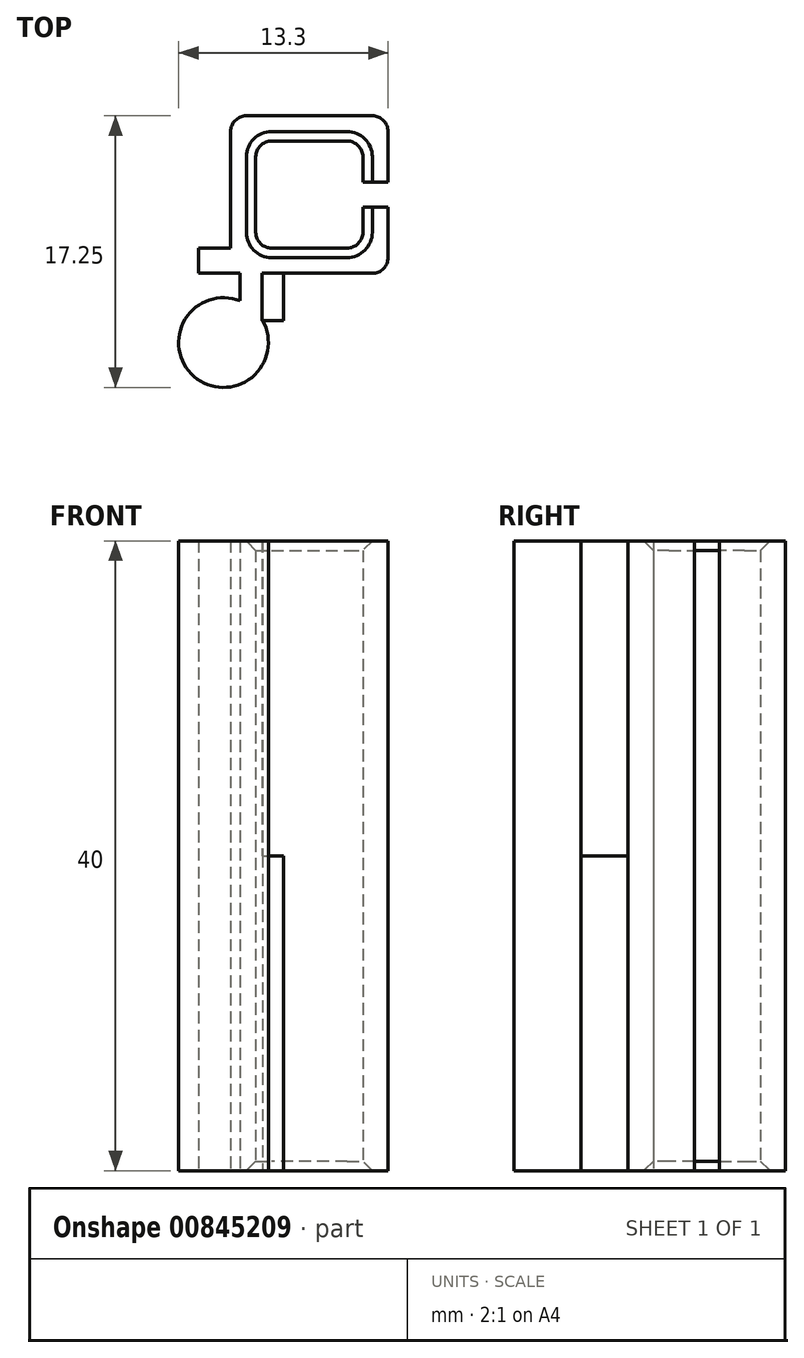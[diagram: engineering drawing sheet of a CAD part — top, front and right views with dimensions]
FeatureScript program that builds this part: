
annotation { "Feature Type Name" : "Feature", "Feature Type Description" : "" }
export const myFeature = defineFeature(function(context is Context, id is Id, definition is map)
    precondition{}
    {
        {
            var Q0;
            Q0=qCreatedBy(makeId("Top.planeOp"),FACE);
            var sketch = newSketch(context, id + "F0", { "sketchPlane" : qUnion([Q0])});
            skCircle(sketch, "E0", {"center": v(0, 0) * mm, "radius": 2.85 * mm});
            skLineSegment(sketch, "E1.bottom", {"start": v(0.45, 0) * mm, "end": v(2.45, 0) * mm});
            skLineSegment(sketch, "E1.top", {"start": v(0.45, 4.4) * mm, "end": v(2.45, 4.4) * mm});
            skLineSegment(sketch, "E1.left", {"start": v(0.45, 0) * mm, "end": v(0.45, 4.4) * mm});
            skLineSegment(sketch, "E1.right", {"start": v(2.45, 0) * mm, "end": v(2.45, 4.4) * mm});
            skLineSegment(sketch, "E2.bottom", {"start": v(0.45, 4.4) * mm, "end": v(10.45, 4.4) * mm});
            skLineSegment(sketch, "E2.top", {"start": v(0.45, 14.4) * mm, "end": v(10.45, 14.4) * mm});
            skLineSegment(sketch, "E2.left", {"start": v(0.45, 4.4) * mm, "end": v(0.45, 14.4) * mm});
            skLineSegment(sketch, "E2.right", {"start": v(10.45, 4.4) * mm, "end": v(10.45, 14.4) * mm});
            skLineSegment(sketch, "E3.bottom", {"start": v(2.05, 6) * mm, "end": v(8.85, 6) * mm});
            skLineSegment(sketch, "E3.top", {"start": v(2.05, 12.8) * mm, "end": v(8.85, 12.8) * mm});
            skLineSegment(sketch, "E3.left", {"start": v(2.05, 6) * mm, "end": v(2.05, 12.8) * mm});
            skLineSegment(sketch, "E3.right", {"start": v(8.85, 6) * mm, "end": v(8.85, 12.8) * mm});
            skLineSegment(sketch, "E4.bottom", {"start": v(8.85, 8.6) * mm, "end": v(10.45, 8.6) * mm});
            skLineSegment(sketch, "E4.top", {"start": v(8.85, 10.2) * mm, "end": v(10.45, 10.2) * mm});
            skLineSegment(sketch, "E4.left", {"start": v(8.85, 8.6) * mm, "end": v(8.85, 10.2) * mm});
            skLineSegment(sketch, "E4.right", {"start": v(10.45, 8.6) * mm, "end": v(10.45, 10.2) * mm});
            skLineSegment(sketch, "E5.bottom", {"start": v(0.45, 4.4) * mm, "end": v(1.05, 4.4) * mm});
            skLineSegment(sketch, "E5.top", {"start": v(0.45, 2.65) * mm, "end": v(1.05, 2.65) * mm});
            skLineSegment(sketch, "E5.left", {"start": v(0.45, 4.4) * mm, "end": v(0.45, 2.65) * mm});
            skLineSegment(sketch, "E5.right", {"start": v(1.05, 4.4) * mm, "end": v(1.05, 2.65) * mm});
            skLineSegment(sketch, "E6.bottom", {"start": v(0.45, 4.4) * mm, "end": v(-1.6, 4.4) * mm});
            skLineSegment(sketch, "E6.top", {"start": v(0.45, 6) * mm, "end": v(-1.6, 6) * mm});
            skLineSegment(sketch, "E6.left", {"start": v(0.45, 4.4) * mm, "end": v(0.45, 6) * mm});
            skLineSegment(sketch, "E6.right", {"start": v(-1.6, 4.4) * mm, "end": v(-1.6, 6) * mm});
            skLineSegment(sketch, "E7.bottom", {"start": v(3.8, 4.4) * mm, "end": v(5.4, 4.4) * mm});
            skLineSegment(sketch, "E7.top", {"start": v(3.8, -1) * mm, "end": v(5.4, -1) * mm});
            skLineSegment(sketch, "E7.left", {"start": v(3.8, 4.4) * mm, "end": v(3.8, -1) * mm});
            skLineSegment(sketch, "E7.right", {"start": v(5.4, 4.4) * mm, "end": v(5.4, -1) * mm});
            skLineSegment(sketch, "E8", {"start": v(2.45, 1.4) * mm, "end": v(3.8, 1.4) * mm});
            skCircle(sketch, "E9", {"center": v(0, 0) * mm, "radius": 3 * mm, "construction": true});
            skLineSegment(sketch, "E10.bottom", {"start": v(3.4, 4) * mm, "end": v(-6.83, 4) * mm, "construction": true});
            skLineSegment(sketch, "E10.top", {"start": v(3.4, -6.58) * mm, "end": v(-6.83, -6.58) * mm, "construction": true});
            skLineSegment(sketch, "E10.left", {"start": v(3.4, 4) * mm, "end": v(3.4, -6.58) * mm, "construction": true});
            skLineSegment(sketch, "E10.right", {"start": v(-6.83, 4) * mm, "end": v(-6.83, -6.58) * mm, "construction": true});
            skLineSegment(sketch, "E11", {"start": v(10.45, 9.4) * mm, "end": v(8.85, 9.4) * mm, "construction": true});
            skSolve(sketch);
        }
        {
            var Q0;
            Q0=makeQuery(id+"F0.imprint","IMPRINT",FACE,{"disambiguationData":[TD([[makeQuery(id+"F0.imprint","IMPRINT",EDGE,{"derivedFrom":sQuery(id+"F0.wireOp",EDGE,"E2.top")}),-1.0]])]});
            var Q1;
            {var subQ5=sQuery(id+"F0.wireOp",EDGE,"E1.bottom");Q1=makeQuery(id+"F0.imprint","IMPRINT",FACE,{"disambiguationData":[TD([[makeQuery(id+"F0.imprint","IMPRINT",EDGE,{"derivedFrom":subQ5}),1.0]])]});}
            var Q2;
            {var subQ5=sQuery(id+"F0.wireOp",EDGE,"E1.bottom");Q2=makeQuery(id+"F0.imprint","IMPRINT",FACE,{"disambiguationData":[TD([[makeQuery(id+"F0.imprint","IMPRINT",EDGE,{"derivedFrom":subQ5}),-1.0]])]});}
            var Q3;
            {var subQ0=sQuery(id+"F0.wireOp",EDGE,"E5.right");Q3=makeQuery(id+"F0.imprint","IMPRINT",FACE,{"disambiguationData":[TD([[makeQuery(id+"F0.imprint","IMPRINT",EDGE,{"derivedFrom":subQ0}),1.0]])]});}
            var Q4;
            {var subQ0=sQuery(id+"F0.wireOp",EDGE,"E5.top");Q4=makeQuery(id+"F0.imprint","IMPRINT",FACE,{"disambiguationData":[TD([[makeQuery(id+"F0.imprint","IMPRINT",EDGE,{"derivedFrom":subQ0}),1.0]])]});}
            var Q5;
            Q5=makeQuery(id+"F0.imprint","IMPRINT",FACE,{"disambiguationData":[TD([[makeQuery(id+"F0.imprint","IMPRINT",EDGE,{"derivedFrom":sQuery(id+"F0.wireOp",EDGE,"E6.bottom")}),-1.0]])]});
            extrude(context, id + "F1", {"entities" : qUnion([Q0, Q1, Q2, Q3, Q4, Q5]), "depth" : 40 * mm, "offsetDistance" : 25 * mm});
        }
        {
            var Q0;
            {var subQ3=sQuery(id+"F0.wireOp",EDGE,"E7.bottom");Q0=makeQuery(id+"F0.imprint","IMPRINT",FACE,{"disambiguationData":[TD([[makeQuery(id+"F0.imprint","IMPRINT",EDGE,{"derivedFrom":subQ3}),-1.0]])]});}
            var Q1;
            {var subQ3=sQuery(id+"F0.wireOp",EDGE,"E8");Q1=makeQuery(id+"F0.imprint","IMPRINT",FACE,{"disambiguationData":[TD([[makeQuery(id+"F0.imprint","IMPRINT",EDGE,{"derivedFrom":subQ3}),1.0]])]});}
            var Q2;
            {var subQ3=sQuery(id+"F0.wireOp",EDGE,"E8");var subQ7=sQuery(id+"F0.wireOp",EDGE,"E0");var subQ9=makeQuery(id+"F0.imprint","INTERSECT",VERTEX,{"derivedFrom":[subQ7,subQ3]});Q2=makeQuery(id+"F0.imprint","IMPRINT",FACE,{"disambiguationData":[TD([[makeQuery(id+"F0.imprint","IMPRINT",EDGE,{"disambiguationData":[TD([[subQ9,-1.0]])],"derivedFrom":subQ7}),-1.0]])]});}
            extrude(context, id + "F2", {"entities" : qUnion([Q0, Q1, Q2]), "operationType" : NewBodyOperationType.ADD, "depth" : 20 * mm, "offsetDistance" : 25 * mm});
        }
        {
            var Q0;
            Q0=makeQuery(id+"F1.opExtrude","SWEPT_EDGE",EDGE,{"disambiguationData":[OSD([sQuery(id+"F0.wireOp",EDGE,"E2.top"),sQuery(id+"F0.wireOp",EDGE,"E2.right")])]});
            var Q1;
            Q1=makeQuery(id+"F1.opExtrude","SWEPT_EDGE",EDGE,{"disambiguationData":[OSD([sQuery(id+"F0.wireOp",EDGE,"E2.top"),sQuery(id+"F0.wireOp",EDGE,"E2.left")])]});
            var Q2;
            Q2=makeQuery(id+"F1.opExtrude","SWEPT_EDGE",EDGE,{"disambiguationData":[OSD([sQuery(id+"F0.wireOp",EDGE,"E2.bottom"),sQuery(id+"F0.wireOp",EDGE,"E2.right")])]});
            var Q3;
            Q3=makeQuery(id+"F1.opExtrude","SWEPT_EDGE",EDGE,{"disambiguationData":[OSD([sQuery(id+"F0.wireOp",EDGE,"E3.top"),sQuery(id+"F0.wireOp",EDGE,"E3.left")])]});
            var Q4;
            Q4=makeQuery(id+"F1.opExtrude","SWEPT_EDGE",EDGE,{"disambiguationData":[OSD([sQuery(id+"F0.wireOp",EDGE,"E3.top"),sQuery(id+"F0.wireOp",EDGE,"E3.right")])]});
            var Q5;
            Q5=makeQuery(id+"F1.opExtrude","SWEPT_EDGE",EDGE,{"disambiguationData":[OSD([sQuery(id+"F0.wireOp",EDGE,"E3.bottom"),sQuery(id+"F0.wireOp",EDGE,"E3.right")])]});
            var Q6;
            Q6=makeQuery(id+"F1.opExtrude","SWEPT_EDGE",EDGE,{"disambiguationData":[OSD([sQuery(id+"F0.wireOp",EDGE,"E3.bottom"),sQuery(id+"F0.wireOp",EDGE,"E3.left")])]});
            fillet(context, id + "F3", {"entities" : qUnion([Q0, Q1, Q2, Q3, Q4, Q5, Q6]), "radius" : 1 * mm, "tangentPropagation" : true, "allowEdgeOverflow" : false});
        }
        {
            var Q0;
            Q0=makeQuery(id+"F1.opExtrude","CAP_EDGE",EDGE,{"disambiguationData":[OSD([sQuery(id+"F0.wireOp",EDGE,"E3.left")])],"isStart":false});
            var Q1;
            Q1=makeQuery(id+"F1.opExtrude","CAP_EDGE",EDGE,{"disambiguationData":[OSD([sQuery(id+"F0.wireOp",EDGE,"E3.bottom")])],"isStart":true});
            chamfer(context, id + "F4", {"entities" : qUnion([Q0, Q1]), "width" : 0.6 * mm, "tangentPropagation" : true});
        }
    });
